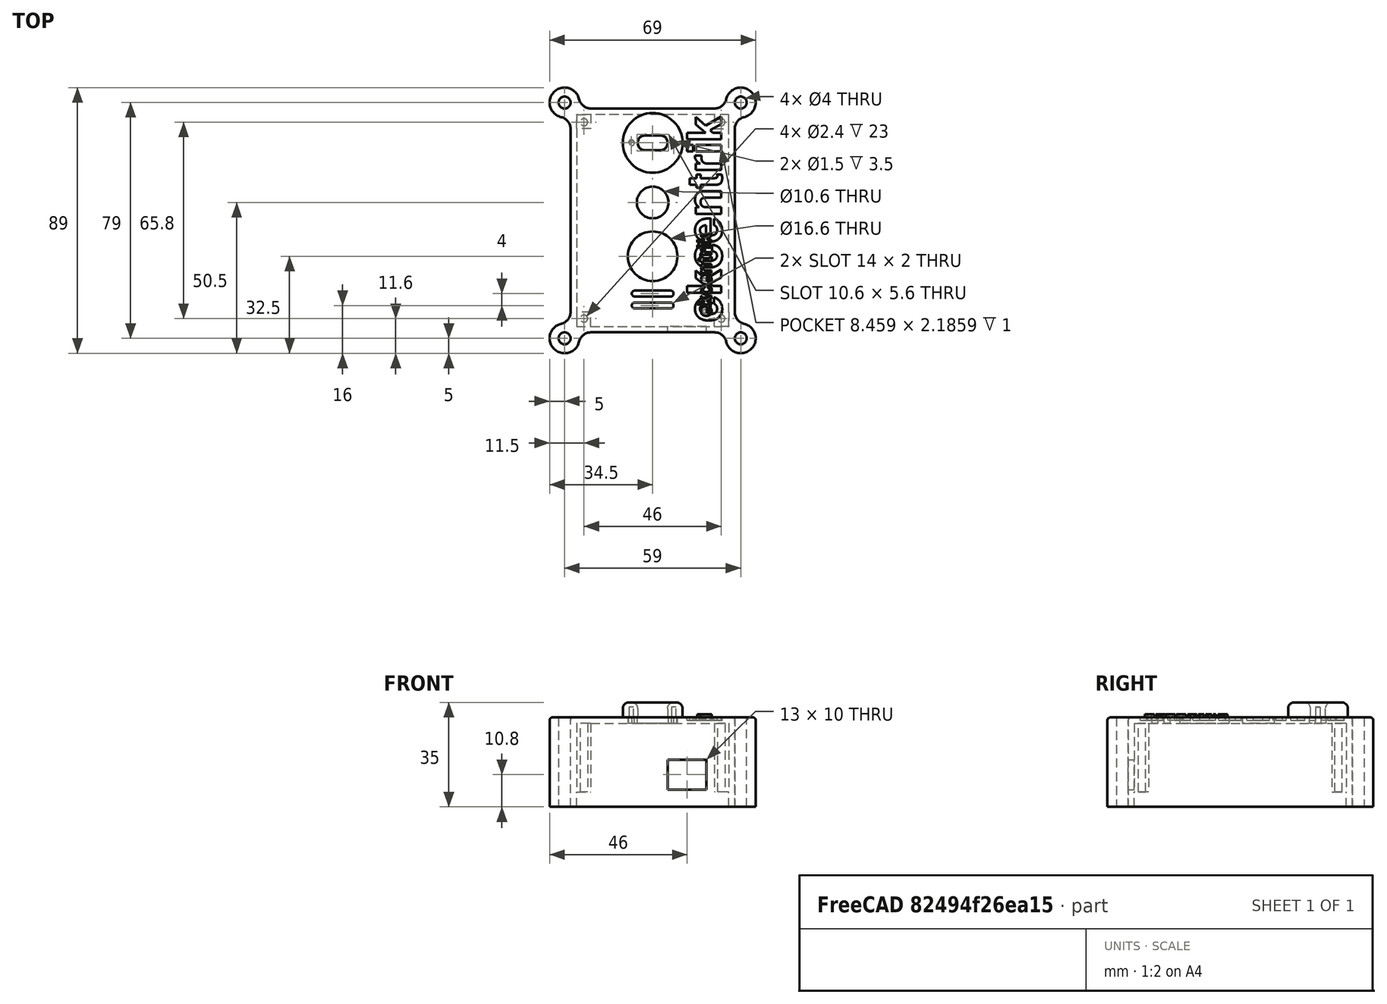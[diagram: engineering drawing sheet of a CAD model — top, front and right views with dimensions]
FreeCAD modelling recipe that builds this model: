
FCSTD DOCUMENT  (FreeCAD 0.18R16110 (Git))
Label: Boitier_V3
License: All rights reserved
LicenseURL: http://en.wikipedia.org/wiki/All_rights_reserved
objects: Sketcher::SketchObject×13, Part::Extrusion×13, Part::Feature×12, PartDesign::Pocket×7, PartDesign::Pad×6, PartDesign::Fillet×4, PartDesign::Body×2, Part::Part2DObjectPython×2, PartDesign::ShapeBinder×1, Mesh::Feature×1, Part::Compound×1, Part::Cut×1
note: 75 computed .brp shape members not serialized (recipe doc carries the construction recipe); baked Part::Feature solids carry a one-line shape summary decoded from their .brp

FEATURE [Sketcher::SketchObject] Sketch
  MapMode = 5
  Support = -> [XY_Plane]
  sketch-geometry (12):
    g0: ArcOfCircle CenterX=-29.5 CenterY=39.5 CenterZ=0 NormalX=0 NormalY=0 NormalZ=1 AngleXU=0 Radius=5 StartAngle=5.87167 EndAngle=11.4071
    g1: ArcOfCircle CenterX=29.5 CenterY=39.5 CenterZ=0 NormalX=0 NormalY=0 NormalZ=1 AngleXU=0 Radius=5 StartAngle=4.30087 EndAngle=9.83629
    g2: ArcOfCircle CenterX=-29.5 CenterY=-39.5 CenterZ=0 NormalX=0 NormalY=0 NormalZ=1 AngleXU=0 Radius=5 StartAngle=1.15928 EndAngle=6.6947
    g3: ArcOfCircle CenterX=29.5 CenterY=-39.5 CenterZ=0 NormalX=0 NormalY=0 NormalZ=1 AngleXU=0 Radius=5 StartAngle=2.73008 EndAngle=8.2655
    g4: LineSegment StartX=27.5 StartY=34.9174 StartZ=0 EndX=27.5 EndY=-34.9174 EndZ=0
    g5: LineSegment StartX=-27.5 StartY=34.9174 StartZ=0 EndX=-27.5 EndY=-34.9174 EndZ=0
    g6: LineSegment StartX=-24.9174 StartY=-37.5 StartZ=0 EndX=24.9174 EndY=-37.5 EndZ=0
    g7: LineSegment StartX=-24.9174 StartY=37.5 StartZ=0 EndX=24.9174 EndY=37.5 EndZ=0
    g8: Circle CenterX=-29.5 CenterY=39.5 CenterZ=0 NormalX=0 NormalY=0 NormalZ=1 AngleXU=0 Radius=2
    g9: Circle CenterX=29.5 CenterY=39.5 CenterZ=0 NormalX=0 NormalY=0 NormalZ=1 AngleXU=0 Radius=2
    g10: Circle CenterX=-29.5 CenterY=-39.5 CenterZ=0 NormalX=0 NormalY=0 NormalZ=1 AngleXU=0 Radius=2
    g11: Circle CenterX=29.5 CenterY=-39.5 CenterZ=0 NormalX=0 NormalY=0 NormalZ=1 AngleXU=0 Radius=2
  constraints (31):
    c: Coincident(g4,g1)
    c: Coincident(g4,g3)
    c: Vertical(g4)
    c: Coincident(g5,g0)
    c: Coincident(g5,g2)
    c: Vertical(g5)
    c: Coincident(g6,g2)
    c: Coincident(g6,g3)
    c: Horizontal(g6)
    c: Coincident(g7,g0)
    c: Horizontal(g7)
    c: Symmetric(g0,g2,g-1)
    c: Symmetric(g1,g3,g-1)
    c: Symmetric(g1,g0,g-2)
    c: Radius(g0) = 5
    c: Equal(g0,g3)
    c: Symmetric(g0,g1,g-2)
    c: Symmetric(g0,g2,g-1)
    c: DistanceX(g-2,g0) = -27.5
    c: DistanceY(g-1,g0) = 37.5
    c: Coincident(g1,g7)
    c: Distance(g0,g5) = 2
    c: Distance(g0,g7) = 2
    c: Coincident(g8,g0)
    c: Coincident(g9,g1)
    c: Coincident(g10,g2)
    c: Coincident(g11,g3)
    c: Radius(g11) = 2
    c: Equal(g11,g10)
    c: Equal(g11,g8)
    c: Equal(g11,g9)
FEATURE [PartDesign::Pad] Pad  label="Envelope externe"
  Length = 30
  Length2 = 100
  Profile = -> Sketch
  Type = 0
FEATURE [Sketcher::SketchObject] Sketch001
  MapMode = 5
  Placement = pos=(0,0,0) rot=(1,0,0;3.14159rad)
  Support = -> [Pad]
  sketch-geometry (4):
    g0: LineSegment StartX=-25.5 StartY=35.5 StartZ=0 EndX=25.5 EndY=35.5 EndZ=0
    g1: LineSegment StartX=25.5 StartY=35.5 StartZ=0 EndX=25.5 EndY=-35.5 EndZ=0
    g2: LineSegment StartX=25.5 StartY=-35.5 StartZ=0 EndX=-25.5 EndY=-35.5 EndZ=0
    g3: LineSegment StartX=-25.5 StartY=-35.5 StartZ=0 EndX=-25.5 EndY=35.5 EndZ=0
  constraints (10):
    c: Coincident(g0,g1)
    c: Coincident(g1,g2)
    c: Coincident(g2,g3)
    c: Coincident(g3,g0)
    c: Horizontal(g2)
    c: Vertical(g1)
    c: Symmetric(g0,g2,g-1)
    c: Symmetric(g0,g0,g-2)
    c: DistanceX(g0,g0) = 51
    c: DistanceY(g1,g1) = 71
FEATURE [PartDesign::Pocket] Pocket  label="Cavite interne"
  BaseFeature = -> Pad
  Length = 28
  Length2 = 100
  Profile = -> Sketch001
  Type = 0
FEATURE [Sketcher::SketchObject] Sketch002
  ExternalGeometry = -> [Pocket]
  MapMode = 5
  Placement = pos=(0,0,28) rot=(1,0,0;3.14159rad)
  Support = -> [Pocket]
  sketch-geometry (5):
    g0: Circle CenterX=-23 CenterY=32.9 CenterZ=0 NormalX=0 NormalY=0 NormalZ=1 AngleXU=0 Radius=1.2
    g1: LineSegment StartX=-25.5 StartY=35.5 StartZ=0 EndX=-20.7 EndY=35.5 EndZ=0
    g2: LineSegment StartX=-20.7 StartY=35.5 StartZ=0 EndX=-20.7 EndY=30.7 EndZ=0
    g3: LineSegment StartX=-20.7 StartY=30.7 StartZ=0 EndX=-25.5 EndY=30.7 EndZ=0
    g4: LineSegment StartX=-25.5 StartY=30.7 StartZ=0 EndX=-25.5 EndY=35.5 EndZ=0
  constraints (14):
    c: Coincident(g1,g2)
    c: Coincident(g2,g3)
    c: Coincident(g3,g4)
    c: Coincident(g4,g1)
    c: Horizontal(g1)
    c: Horizontal(g3)
    c: Vertical(g2)
    c: Vertical(g4)
    c: Coincident(g1,g-4)
    c: Radius(g0) = 1.2
    c: Distance(g3) = 4.8
    c: DistanceX(g-2,g0) = -23
    c: DistanceY(g-1,g0) = 32.9
    c: Distance(g2) = 4.8
FEATURE [PartDesign::Pad] Pad001  label="Pilier PCB 1"
  BaseFeature = -> Pocket
  Length = 23
  Length2 = 100
  Profile = -> Sketch002
  Type = 0
FEATURE [Sketcher::SketchObject] Sketch003
  ExternalGeometry = -> [Pad001]
  MapMode = 5
  Placement = pos=(0,0,28) rot=(1,0,0;3.14159rad)
  Support = -> [Pad001]
  sketch-geometry (5):
    g0: LineSegment StartX=25.5 StartY=35.5 StartZ=0 EndX=20.7 EndY=35.5 EndZ=0
    g1: LineSegment StartX=20.7 StartY=35.5 StartZ=0 EndX=20.7 EndY=30.7 EndZ=0
    g2: LineSegment StartX=20.7 StartY=30.7 StartZ=0 EndX=25.5 EndY=30.7 EndZ=0
    g3: LineSegment StartX=25.5 StartY=30.7 StartZ=0 EndX=25.5 EndY=35.5 EndZ=0
    g4: Circle CenterX=23 CenterY=32.9 CenterZ=0 NormalX=0 NormalY=0 NormalZ=1 AngleXU=0 Radius=1.2
  constraints (14):
    c: Coincident(g0,g1)
    c: Coincident(g1,g2)
    c: Coincident(g2,g3)
    c: Coincident(g3,g0)
    c: Horizontal(g0)
    c: Horizontal(g2)
    c: Vertical(g1)
    c: Vertical(g3)
    c: Coincident(g0,g-4)
    c: DistanceY(g1,g1) = 4.8
    c: DistanceX(g2,g2) = 4.8
    c: Radius(g4) = 1.2
    c: DistanceX(g-2,g4) = 23
    c: DistanceY(g-1,g4) = 32.9
FEATURE [PartDesign::Pad] Pad002  label="Pilier PCB 2"
  BaseFeature = -> Pad001
  Length = 23
  Length2 = 100
  Profile = -> Sketch003
  Type = 0
FEATURE [Sketcher::SketchObject] Sketch004
  ExternalGeometry = -> [Pad002]
  MapMode = 5
  Placement = pos=(0,0,28) rot=(1,0,0;3.14159rad)
  Support = -> [Pad002]
  sketch-geometry (5):
    g0: LineSegment StartX=25.5 StartY=-35.5 StartZ=0 EndX=20.7 EndY=-35.5 EndZ=0
    g1: LineSegment StartX=20.7 StartY=-35.5 StartZ=0 EndX=20.7 EndY=-30.7 EndZ=0
    g2: LineSegment StartX=20.7 StartY=-30.7 StartZ=0 EndX=25.5 EndY=-30.7 EndZ=0
    g3: LineSegment StartX=25.5 StartY=-30.7 StartZ=0 EndX=25.5 EndY=-35.5 EndZ=0
    g4: Circle CenterX=23 CenterY=-32.9 CenterZ=0 NormalX=0 NormalY=0 NormalZ=1 AngleXU=0 Radius=1.2
  constraints (14):
    c: Coincident(g0,g1)
    c: Coincident(g1,g2)
    c: Coincident(g2,g3)
    c: Coincident(g3,g0)
    c: Horizontal(g0)
    c: Horizontal(g2)
    c: Vertical(g1)
    c: Vertical(g3)
    c: Coincident(g0,g-4)
    c: DistanceX(g2,g2) = 4.8
    c: DistanceY(g1,g1) = 4.8
    c: Radius(g4) = 1.2
    c: DistanceX(g-2,g4) = 23
    c: DistanceY(g-1,g4) = -32.9
FEATURE [PartDesign::Pad] Pad003  label="Pilier PCB 3"
  BaseFeature = -> Pad002
  Length = 23
  Length2 = 100
  Profile = -> Sketch004
  Type = 0
FEATURE [Sketcher::SketchObject] Sketch005
  ExternalGeometry = -> [Pad003]
  MapMode = 5
  Placement = pos=(0,0,28) rot=(1,0,0;3.14159rad)
  Support = -> [Pad003]
  sketch-geometry (5):
    g0: LineSegment StartX=-25.5 StartY=-35.5 StartZ=0 EndX=-20.7 EndY=-35.5 EndZ=0
    g1: LineSegment StartX=-20.7 StartY=-35.5 StartZ=0 EndX=-20.7 EndY=-30.7 EndZ=0
    g2: LineSegment StartX=-20.7 StartY=-30.7 StartZ=0 EndX=-25.5 EndY=-30.7 EndZ=0
    g3: LineSegment StartX=-25.5 StartY=-30.7 StartZ=0 EndX=-25.5 EndY=-35.5 EndZ=0
    g4: Circle CenterX=-23 CenterY=-32.9 CenterZ=0 NormalX=0 NormalY=0 NormalZ=1 AngleXU=0 Radius=1.2
  constraints (14):
    c: Coincident(g0,g1)
    c: Coincident(g1,g2)
    c: Coincident(g2,g3)
    c: Coincident(g3,g0)
    c: Horizontal(g0)
    c: Horizontal(g2)
    c: Vertical(g1)
    c: Vertical(g3)
    c: Coincident(g0,g-4)
    c: DistanceX(g2,g2) = 4.8
    c: DistanceY(g1,g1) = 4.8
    c: Radius(g4) = 1.2
    c: DistanceX(g-2,g4) = -23
    c: DistanceY(g-1,g4) = -32.9
FEATURE [PartDesign::Pad] Pad004  label="Pilier PCB 4"
  BaseFeature = -> Pad003
  Length = 23
  Length2 = 100
  Profile = -> Sketch005
  Type = 0
FEATURE [Sketcher::SketchObject] Sketch006
  ExternalGeometry = -> [Pad004]
  MapMode = 5
  Placement = pos=(0,0,28) rot=(1,0,0;3.14159rad)
  Support = -> [Pad004]
  sketch-geometry (1):
    g0: Circle CenterX=0 CenterY=-6 CenterZ=0 NormalX=0 NormalY=0 NormalZ=1 AngleXU=0 Radius=5.3
  constraints (3):
    c: PointOnObject(g0,g-2)
    c: Distance(g0,g-3) = 41.5
    c: Radius(g0) = 5.3
FEATURE [PartDesign::Pocket] Pocket001  label="Percage LED"
  BaseFeature = -> Pad004
  Length = 5
  Length2 = 100
  Profile = -> Sketch006
  Type = 0
FEATURE [Sketcher::SketchObject] Sketch007
  MapMode = 5
  Placement = pos=(0,0,28) rot=(1,0,0;3.14159rad)
  Support = -> [Pocket001]
  sketch-geometry (1):
    g0: Circle CenterX=0 CenterY=12 CenterZ=0 NormalX=0 NormalY=0 NormalZ=1 AngleXU=0 Radius=8.3
  constraints (3):
    c: PointOnObject(g0,g-2)
    c: Radius(g0) = 8.3
    c: DistanceY(g-1,g0) = 12
FEATURE [PartDesign::Pocket] Pocket002  label="Percage bouton"
  BaseFeature = -> Pocket001
  Length = 5
  Length2 = 100
  Profile = -> Sketch007
  Type = 0
FEATURE [Sketcher::SketchObject] Sketch008
  ExternalGeometry = -> [Pocket002]
  MapMode = 5
  Placement = pos=(0,0,28) rot=(1,0,0;3.14159rad)
  Support = -> [Pocket002]
  sketch-geometry (8):
    g0: ArcOfCircle CenterX=-6 CenterY=28.5 CenterZ=0 NormalX=0 NormalY=0 NormalZ=1 AngleXU=0 Radius=1 StartAngle=1.5708 EndAngle=4.71239
    g1: ArcOfCircle CenterX=6 CenterY=28.5 CenterZ=0 NormalX=0 NormalY=0 NormalZ=1 AngleXU=0 Radius=1 StartAngle=4.71239 EndAngle=7.85398
    g2: LineSegment StartX=-6 StartY=27.5 StartZ=0 EndX=6 EndY=27.5 EndZ=0
    g3: LineSegment StartX=-6 StartY=29.5 StartZ=0 EndX=6 EndY=29.5 EndZ=0
    g4: ArcOfCircle CenterX=-6 CenterY=24.5 CenterZ=0 NormalX=0 NormalY=0 NormalZ=1 AngleXU=0 Radius=1 StartAngle=1.5708 EndAngle=4.71239
    g5: ArcOfCircle CenterX=6 CenterY=24.5 CenterZ=0 NormalX=0 NormalY=0 NormalZ=1 AngleXU=0 Radius=1 StartAngle=4.71239 EndAngle=7.85398
    g6: LineSegment StartX=-6 StartY=23.5 StartZ=0 EndX=6 EndY=23.5 EndZ=0
    g7: LineSegment StartX=-6 StartY=25.5 StartZ=0 EndX=6 EndY=25.5 EndZ=0
  constraints (18):
    c: Tangent(g0,g3) = 1.5708
    c: Tangent(g0,g2) = -1.5708
    c: Tangent(g2,g1) = -1.5708
    c: Tangent(g3,g1) = 1.5708
    c: Horizontal(g2)
    c: Tangent(g4,g7) = 1.5708
    c: Tangent(g4,g6) = -1.5708
    c: Tangent(g6,g5) = -1.5708
    c: Tangent(g7,g5) = 1.5708
    c: Horizontal(g6)
    c: Symmetric(g0,g1,g-2)
    c: Symmetric(g4,g5,g-2)
    c: Radius(g1) = 1
    c: Radius(g5) = 1
    c: Distance(g1,g7) = 2
    c: Distance(g3) = 12
    c: Distance(g7) = 12
    c: Distance(g1,g-3) = 6
FEATURE [PartDesign::Pocket] Pocket003  label="Percage buzzer"
  BaseFeature = -> Pocket002
  Length = 5
  Length2 = 100
  Profile = -> Sketch008
  Type = 0
FEATURE [Sketcher::SketchObject] Sketch009
  ExternalGeometry = -> [Pocket003]
  MapMode = 5
  Placement = pos=(0,-37.5,0) rot=(1,0,0;1.5708rad)
  Support = -> [Pocket003]
  sketch-geometry (4):
    g0: LineSegment StartX=5 StartY=15.8 StartZ=0 EndX=18 EndY=15.8 EndZ=0
    g1: LineSegment StartX=18 StartY=15.8 StartZ=0 EndX=18 EndY=5.8 EndZ=0
    g2: LineSegment StartX=18 StartY=5.8 StartZ=0 EndX=5 EndY=5.8 EndZ=0
    g3: LineSegment StartX=5 StartY=5.8 StartZ=0 EndX=5 EndY=15.8 EndZ=0
  constraints (12):
    c: Coincident(g0,g1)
    c: Coincident(g1,g2)
    c: Coincident(g2,g3)
    c: Coincident(g3,g0)
    c: Horizontal(g0)
    c: Horizontal(g2)
    c: Vertical(g1)
    c: Vertical(g3)
    c: DistanceX(g0,g0) = 13
    c: DistanceY(g1,g1) = 10
    c: DistanceX(g-2,g2) = 5
    c: Distance(g1,g-3) = 0.8
FEATURE [PartDesign::Pocket] Pocket004  label="Percage USB"
  BaseFeature = -> Pocket003
  Length = 5
  Length2 = 100
  Profile = -> Sketch009
  Type = 0
FEATURE [Sketcher::SketchObject] Sketch010
  ExternalGeometry = -> [Pocket004]
  MapMode = 5
  Placement = pos=(0,0,28) rot=(1,0,0;3.14159rad)
  Support = -> [Pocket004]
  sketch-geometry (6):
    g0: ArcOfCircle CenterX=-2.5 CenterY=-26 CenterZ=0 NormalX=0 NormalY=0 NormalZ=1 AngleXU=0 Radius=2.8 StartAngle=1.5708 EndAngle=4.71239
    g1: ArcOfCircle CenterX=2.5 CenterY=-26 CenterZ=0 NormalX=0 NormalY=0 NormalZ=1 AngleXU=0 Radius=2.8 StartAngle=4.71239 EndAngle=7.85398
    g2: LineSegment StartX=-2.5 StartY=-28.8 StartZ=0 EndX=2.5 EndY=-28.8 EndZ=0
    g3: LineSegment StartX=-2.5 StartY=-23.2 StartZ=0 EndX=2.5 EndY=-23.2 EndZ=0
    g4: Circle CenterX=-7.115 CenterY=-26 CenterZ=0 NormalX=0 NormalY=0 NormalZ=1 AngleXU=0 Radius=1
    g5: Circle CenterX=7.115 CenterY=-26 CenterZ=0 NormalX=0 NormalY=0 NormalZ=1 AngleXU=0 Radius=1
  constraints (14):
    c: Tangent(g0,g3) = 1.5708
    c: Tangent(g0,g2) = -1.5708
    c: Tangent(g2,g1) = -1.5708
    c: Tangent(g3,g1) = 1.5708
    c: Horizontal(g2)
    c: Radius(g1) = 2.8
    c: DistanceX(g3,g3) = 5
    c: Symmetric(g0,g1,g-2)
    c: Symmetric(g5,g4,g-2)
    c: DistanceX(g-2,g4) = -7.115
    c: Radius(g4) = 1
    c: Equal(g4,g5)
    c: DistanceY(g-1,g5) = -26
    c: DistanceY(g-1,g1) = -26
FEATURE [PartDesign::Pocket] Pocket005  label="Percage TOF10120"
  BaseFeature = -> Pocket004
  Length = 5
  Length2 = 100
  Profile = -> Sketch010
  Type = 0
FEATURE [PartDesign::ShapeBinder] CopyPocket005
  TraceSupport = false
FEATURE [Sketcher::SketchObject] Sketch011
  MapMode = 5
  Placement = pos=(0,0,30) rot=(0,0,1;0rad)
  Support = -> [CopyPocket005]
  sketch-geometry (5):
    g0: ArcOfCircle CenterX=-2.5 CenterY=26 CenterZ=0 NormalX=0 NormalY=0 NormalZ=1 AngleXU=0 Radius=2.5 StartAngle=1.5708 EndAngle=4.71239
    g1: ArcOfCircle CenterX=2.5 CenterY=26 CenterZ=0 NormalX=0 NormalY=0 NormalZ=1 AngleXU=0 Radius=2.5 StartAngle=4.71239 EndAngle=7.85398
    g2: LineSegment StartX=-2.5 StartY=23.5 StartZ=0 EndX=2.5 EndY=23.5 EndZ=0
    g3: LineSegment StartX=-2.5 StartY=28.5 StartZ=0 EndX=2.5 EndY=28.5 EndZ=0
    g4: Circle CenterX=0.000374 CenterY=26 CenterZ=0 NormalX=0 NormalY=0 NormalZ=1 AngleXU=0 Radius=10
  constraints (11):
    c: Tangent(g0,g3) = 1.5708
    c: Tangent(g0,g2) = -1.5708
    c: Tangent(g2,g1) = -1.5708
    c: Tangent(g3,g1) = 1.5708
    c: Horizontal(g2)
    c: Radius(g1) = 2.5
    c: DistanceX(g3,g3) = 5
    c: Symmetric(g1,g0,g-2)
    c: DistanceY(g-1,g1) = 26
    c: DistanceY(g-1,g4) = 26
    c: Radius(g4) = 10
FEATURE [PartDesign::Pad] Pad005  label="Forme generale"
  Length = 5
  Length2 = 100
  Profile = -> Sketch011
  Type = 0
FEATURE [PartDesign::Fillet] Fillet
  Base = -> Pad005 [Edge15]
  BaseFeature = -> Pad005
  Radius = 2
FEATURE [PartDesign::Fillet] Fillet001
  Base = -> Fillet [Edge22]
  BaseFeature = -> Fillet
  Radius = 2
FEATURE [Sketcher::SketchObject] Sketch012
  MapMode = 5
  Placement = pos=(0,0,30) rot=(1,0,0;3.14159rad)
  Support = -> [Fillet001]
  sketch-geometry (2):
    g0: Circle CenterX=-7.115 CenterY=-26 CenterZ=0 NormalX=0 NormalY=0 NormalZ=1 AngleXU=0 Radius=0.75
    g1: Circle CenterX=7.115 CenterY=-26 CenterZ=0 NormalX=0 NormalY=0 NormalZ=1 AngleXU=0 Radius=0.75
  constraints (5):
    c: Symmetric(g0,g1,g-2)
    c: Radius(g0) = 0.75
    c: Equal(g0,g1)
    c: DistanceY(g-1,g0) = -26
    c: DistanceX(g-2,g0) = -7.115
FEATURE [PartDesign::Pocket] Pocket006
  BaseFeature = -> Fillet001
  Length = 3.5
  Length2 = 100
  Profile = -> Sketch012
  Type = 0
FEATURE [PartDesign::Body] Body001  label="Protecteur TOF"
  Group = -> [CopyPocket005,Sketch011,Pad005,Fillet,Fillet001,Sketch012,Pocket006]
  Origin = -> Origin001
  Tip = -> Pocket006
FEATURE [Mesh::Feature] Mesh  label="Protecteur TOF (Meshed)"
FEATURE [PartDesign::Fillet] Fillet002
  Base = -> Pocket005 [Edge2,Edge1,Edge49,Edge5,Edge50,Edge8,Edge51,Edge52]
  BaseFeature = -> Pocket005
  Radius = 4
FEATURE [PartDesign::Fillet] Fillet003
  Base = -> Fillet002 [Edge40]
  BaseFeature = -> Fillet002
  Radius = 1
FEATURE [PartDesign::Body] Body  label="Boitier PCB"
  Group = -> [Sketch,Pad,Sketch001,Pocket,Sketch002,Pad001,Sketch003,Pad002,Sketch004,Pad003,Sketch005,Pad004,Sketch006,Pocket001,Sketch007,Pocket002,Sketch008,Pocket003,Sketch009,Pocket004,Sketch010,Pocket005,Fillet002,Fillet003]
  Origin = -> Origin
  Tip = -> Fillet003
FEATURE [Part::Feature] Face
  shape: bbox 3.105 x 4.629 x 2e-07 mm, 1 faces, 0 solids (baked)
FEATURE [Part::Feature] Face001
  shape: bbox 0.889 x 0.7938 x 2e-07 mm, 1 faces, 0 solids (baked)
FEATURE [Part::Feature] Face002
  shape: bbox 0.889 x 3.429 x 2e-07 mm, 1 faces, 0 solids (baked)
FEATURE [Part::Feature] Face003
  shape: bbox 1.949 x 3.486 x 2e-07 mm, 1 faces, 0 solids (baked)
FEATURE [Part::Feature] Face004
  shape: bbox 1.822 x 4.426 x 2e-07 mm, 1 faces, 0 solids (baked)
FEATURE [Part::Feature] Face005
  shape: bbox 3.067 x 3.486 x 2e-07 mm, 1 faces, 0 solids (baked)
FEATURE [Part::Feature] Face006
  shape: bbox 1.365 x 0.7811 x 2e-07 mm, 1 faces, 0 solids (baked)
FEATURE [Part::Feature] Face007
  shape: bbox 3.194 x 3.632 x 2e-07 mm, 1 faces, 0 solids (baked)
FEATURE [Part::Feature] Face008
  shape: bbox 3.099 x 3.632 x 2e-07 mm, 1 faces, 0 solids (baked)
FEATURE [Part::Feature] Face009
  shape: bbox 3.105 x 4.629 x 2e-07 mm, 1 faces, 0 solids (baked)
FEATURE [Part::Feature] Face010
  shape: bbox 1.365 x 0.7811 x 2e-07 mm, 1 faces, 0 solids (baked)
FEATURE [Part::Feature] Face011
  shape: bbox 3.194 x 3.632 x 2e-07 mm, 1 faces, 0 solids (baked)
FEATURE [Part::Extrusion] Extrude
  Base = -> Face
  Dir = (0,0,1)
  DirMode = 2
  FaceMakerClass = Part::FaceMakerBullseye
  LengthFwd = 1
  LengthRev = 0
  Solid = false
  Symmetric = false
FEATURE [Part::Extrusion] Extrude001
  Base = -> Face001
  Dir = (0,0,1)
  DirMode = 2
  FaceMakerClass = Part::FaceMakerBullseye
  LengthFwd = 1
  LengthRev = 0
  Solid = false
  Symmetric = false
FEATURE [Part::Extrusion] Extrude002
  Base = -> Face002
  Dir = (0,0,1)
  DirMode = 2
  FaceMakerClass = Part::FaceMakerBullseye
  LengthFwd = 1
  LengthRev = 0
  Solid = false
  Symmetric = false
FEATURE [Part::Extrusion] Extrude003
  Base = -> Face003
  Dir = (0,0,1)
  DirMode = 2
  FaceMakerClass = Part::FaceMakerBullseye
  LengthFwd = 1
  LengthRev = 0
  Solid = false
  Symmetric = false
FEATURE [Part::Extrusion] Extrude004
  Base = -> Face004
  Dir = (0,0,1)
  DirMode = 2
  FaceMakerClass = Part::FaceMakerBullseye
  LengthFwd = 1
  LengthRev = 0
  Solid = false
  Symmetric = false
FEATURE [Part::Extrusion] Extrude005
  Base = -> Face005
  Dir = (0,0,1)
  DirMode = 2
  FaceMakerClass = Part::FaceMakerBullseye
  LengthFwd = 1
  LengthRev = 0
  Solid = false
  Symmetric = false
FEATURE [Part::Extrusion] Extrude006
  Base = -> Face006
  Dir = (0,0,-1)
  DirMode = 2
  FaceMakerClass = Part::FaceMakerBullseye
  LengthFwd = 1
  LengthRev = 0
  Solid = false
  Symmetric = false
FEATURE [Part::Extrusion] Extrude007
  Base = -> Face007
  Dir = (0,0,1)
  DirMode = 2
  FaceMakerClass = Part::FaceMakerBullseye
  LengthFwd = 1
  LengthRev = 0
  Solid = false
  Symmetric = false
FEATURE [Part::Extrusion] Extrude008
  Base = -> Face008
  Dir = (0,0,1)
  DirMode = 2
  FaceMakerClass = Part::FaceMakerBullseye
  LengthFwd = 1
  LengthRev = 0
  Solid = false
  Symmetric = false
FEATURE [Part::Extrusion] Extrude009
  Base = -> Face009
  Dir = (0,0,1)
  DirMode = 2
  FaceMakerClass = Part::FaceMakerBullseye
  LengthFwd = 1
  LengthRev = 0
  Solid = false
  Symmetric = false
FEATURE [Part::Extrusion] Extrude010
  Base = -> Face010
  Dir = (0,0,-1)
  DirMode = 2
  FaceMakerClass = Part::FaceMakerBullseye
  LengthFwd = 1
  LengthRev = 0
  Solid = false
  Symmetric = false
FEATURE [Part::Extrusion] Extrude011
  Base = -> Face011
  Dir = (0,0,1)
  DirMode = 2
  FaceMakerClass = Part::FaceMakerBullseye
  LengthFwd = 1
  LengthRev = 0
  Solid = false
  Symmetric = false
FEATURE [Part::Compound] Compound  label="ekcentrik_texte"
  Links = -> [Extrude,Extrude008,Extrude002,Extrude003,Extrude005,Extrude009,Extrude006,Extrude001,Extrude007,Extrude004,Extrude010,Extrude011]
  Placement = pos=(15,-32,30) rot=(0,0,1;1.5708rad)
FEATURE [Part::Part2DObjectPython] ShapeString002  # Draft 2D object (typed FeaturePython)
  FontFile = <path>
  Placement = pos=(-182.16,-26.36,0) rot=(0,0,1;0rad)
  Size = 8
  String = ekcentrik
  Tracking = 0
FEATURE [Part::Part2DObjectPython] ShapeString  # Draft 2D object (typed FeaturePython)
  FontFile = <path>
  Placement = pos=(15.12,-10.95,0) rot=(0,0,1;0rad)
  Size = 7
  String = ekcentrik
  Tracking = 0
FEATURE [Part::Extrusion] Extrude012
  Base = -> ShapeString
  Dir = (0,0,1)
  DirMode = 2
  FaceMakerClass = Part::FaceMakerBullseye
  LengthFwd = 10
  LengthRev = 0
  Placement = pos=(12,-49,29) rot=(0,0,1;1.5708rad)
  Solid = false
  Symmetric = false
FEATURE [Part::Cut] Cut
  Base = -> Body
  Tool = -> Extrude012
note: 2 file-system paths scrubbed to <path> (originals preserved in the JSON sidecar)
